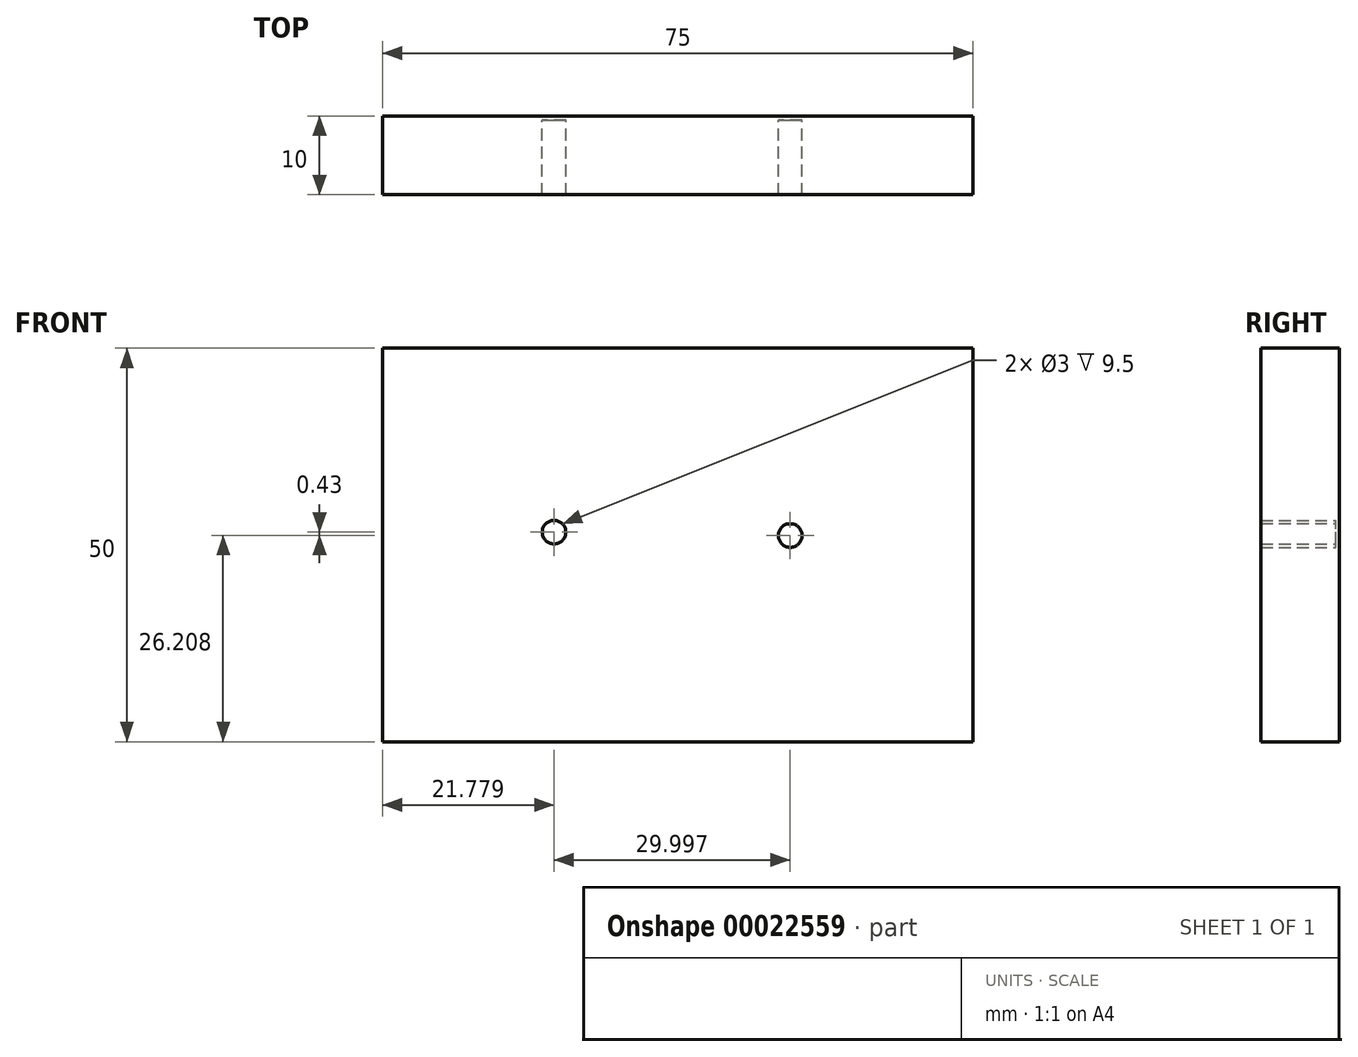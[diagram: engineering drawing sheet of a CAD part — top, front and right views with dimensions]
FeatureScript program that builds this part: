
annotation { "Feature Type Name" : "Feature", "Feature Type Description" : "" }
export const myFeature = defineFeature(function(context is Context, id is Id, definition is map)
    precondition{}
    {
        {
            var Q0;
            Q0=qCreatedBy(makeId("Front.planeOp"),FACE);
            var sketch = newSketch(context, id + "F0", { "sketchPlane" : qUnion([Q0])});
            skLineSegment(sketch, "E0.bottom", {"start": v(-25.28, 15.51) * mm, "end": v(49.72, 15.51) * mm});
            skLineSegment(sketch, "E0.top", {"start": v(-25.28, -34.49) * mm, "end": v(49.72, -34.49) * mm});
            skLineSegment(sketch, "E0.left", {"start": v(-25.28, 15.51) * mm, "end": v(-25.28, -34.49) * mm});
            skLineSegment(sketch, "E0.right", {"start": v(49.72, 15.51) * mm, "end": v(49.72, -34.49) * mm});
            skCircle(sketch, "E1", {"center": v(-3.5, -7.85) * mm, "radius": 1.5 * mm});
            skCircle(sketch, "E2", {"center": v(26.5, -8.28) * mm, "radius": 1.5 * mm});
            skSolve(sketch);
        }
        {
            var Q0;
            Q0=makeQuery(id+"F0.imprint","IMPRINT",FACE,{"disambiguationData":[TD([[makeQuery(id+"F0.imprint","IMPRINT",EDGE,{"derivedFrom":sQuery(id+"F0.wireOp",EDGE,"E0.bottom")}),-1.0]])]});
            extrude(context, id + "F1", {"entities" : qUnion([Q0]), "depth" : 10 * mm});
        }
        {
            var Q0;
            Q0=makeQuery(id+"F0.imprint","IMPRINT",FACE,{"disambiguationData":[TD([[makeQuery(id+"F0.imprint","IMPRINT",EDGE,{"derivedFrom":sQuery(id+"F0.wireOp",EDGE,"E2")}),1.0]])]});
            var Q1;
            Q1=makeQuery(id+"F0.imprint","IMPRINT",FACE,{"disambiguationData":[TD([[makeQuery(id+"F0.imprint","IMPRINT",EDGE,{"derivedFrom":sQuery(id+"F0.wireOp",EDGE,"E1")}),1.0]])]});
            extrude(context, id + "F2", {"entities" : qUnion([Q0, Q1]), "operationType" : NewBodyOperationType.ADD, "depth" : .5 * mm});
        }
    });
